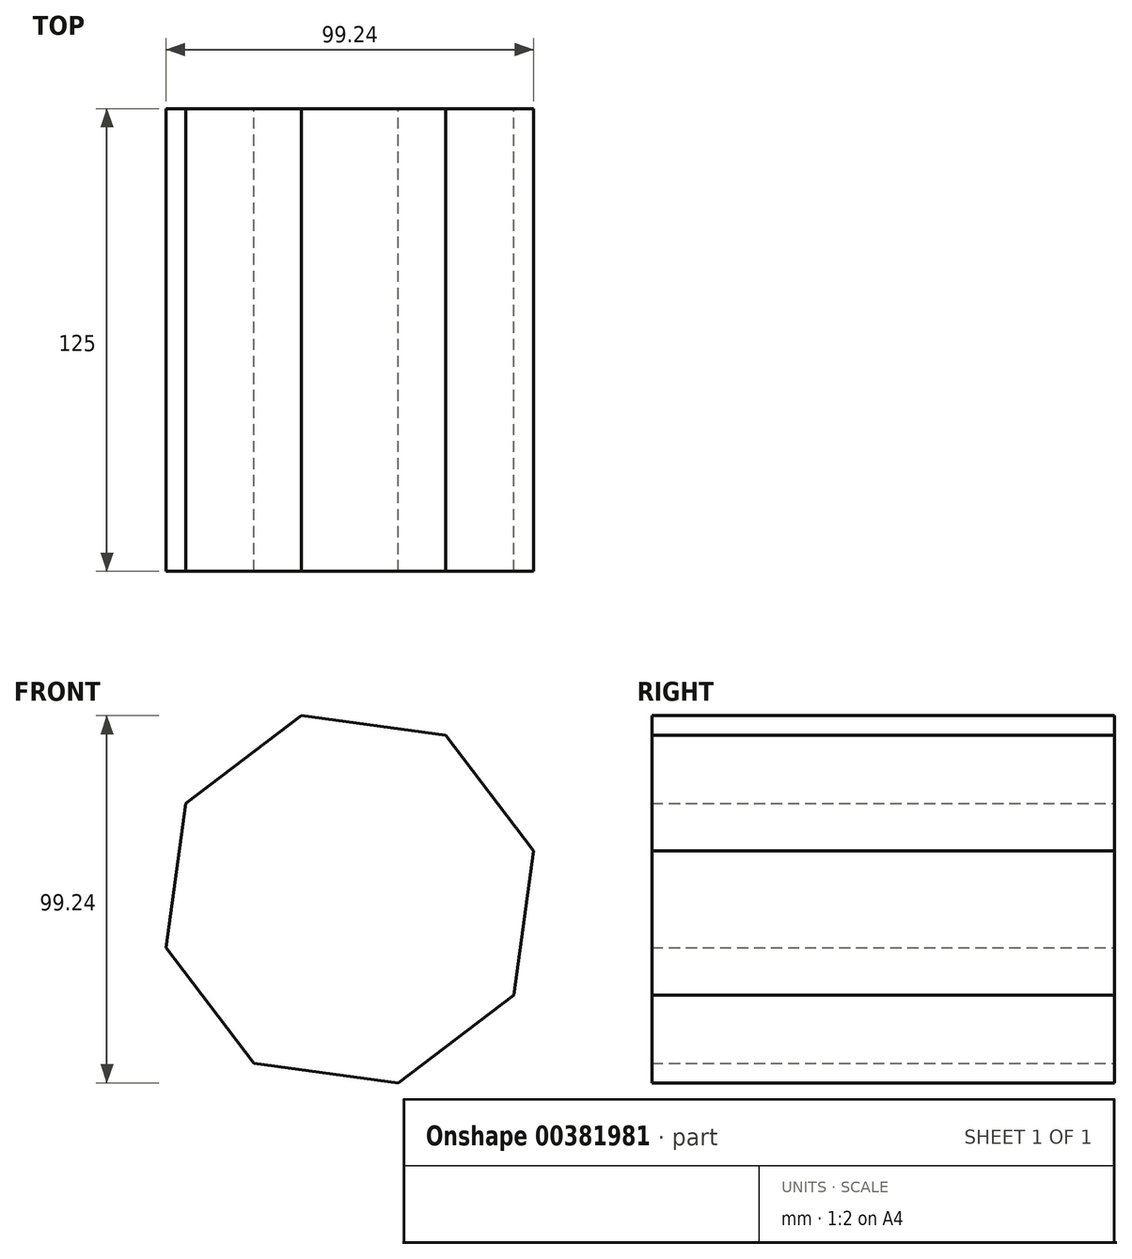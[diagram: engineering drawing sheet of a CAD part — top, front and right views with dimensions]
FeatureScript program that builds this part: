
annotation { "Feature Type Name" : "Feature", "Feature Type Description" : "" }
export const myFeature = defineFeature(function(context is Context, id is Id, definition is map)
    precondition{}
    {
        {
            var Q0;
            Q0=qCreatedBy(makeId("Front.planeOp"),FACE);
            var sketch = newSketch(context, id + "F0", { "sketchPlane" : qUnion([Q0])});
            skCircle(sketch, "E0.cCircle", {"center": v(0, 0) * mm, "radius": 47.4 * mm, "construction": true});
            skLineSegment(sketch, "E0.0", {"start": v(-44.3, 25.87) * mm, "end": v(-13.04, 49.62) * mm});
            skLineSegment(sketch, "E0.1", {"start": v(-13.04, 49.62) * mm, "end": v(25.87, 44.3) * mm});
            skLineSegment(sketch, "E0.2", {"start": v(25.87, 44.3) * mm, "end": v(49.62, 13.04) * mm});
            skLineSegment(sketch, "E0.3", {"start": v(49.62, 13.04) * mm, "end": v(44.3, -25.87) * mm});
            skLineSegment(sketch, "E0.4", {"start": v(44.3, -25.87) * mm, "end": v(13.04, -49.62) * mm});
            skLineSegment(sketch, "E0.5", {"start": v(13.04, -49.62) * mm, "end": v(-25.87, -44.3) * mm});
            skLineSegment(sketch, "E0.6", {"start": v(-25.87, -44.3) * mm, "end": v(-49.62, -13.04) * mm});
            skLineSegment(sketch, "E0.7", {"start": v(-49.62, -13.04) * mm, "end": v(-44.3, 25.87) * mm});
            skPoint(sketch, "E0.0.midPoint", {"position": v(-28.67, 37.74) * mm});
            skSolve(sketch);
        }
        {
            var Q0;
            Q0=makeQuery(id+"F0.imprint","IMPRINT",FACE,{"disambiguationData":[TD([[makeQuery(id+"F0.imprint","IMPRINT",EDGE,{"derivedFrom":sQuery(id+"F0.wireOp",EDGE,"E0.0")}),-1.0]])]});
            extrude(context, id + "F1", {"entities" : qUnion([Q0]), "depth" : 125 * mm});
        }
    });
